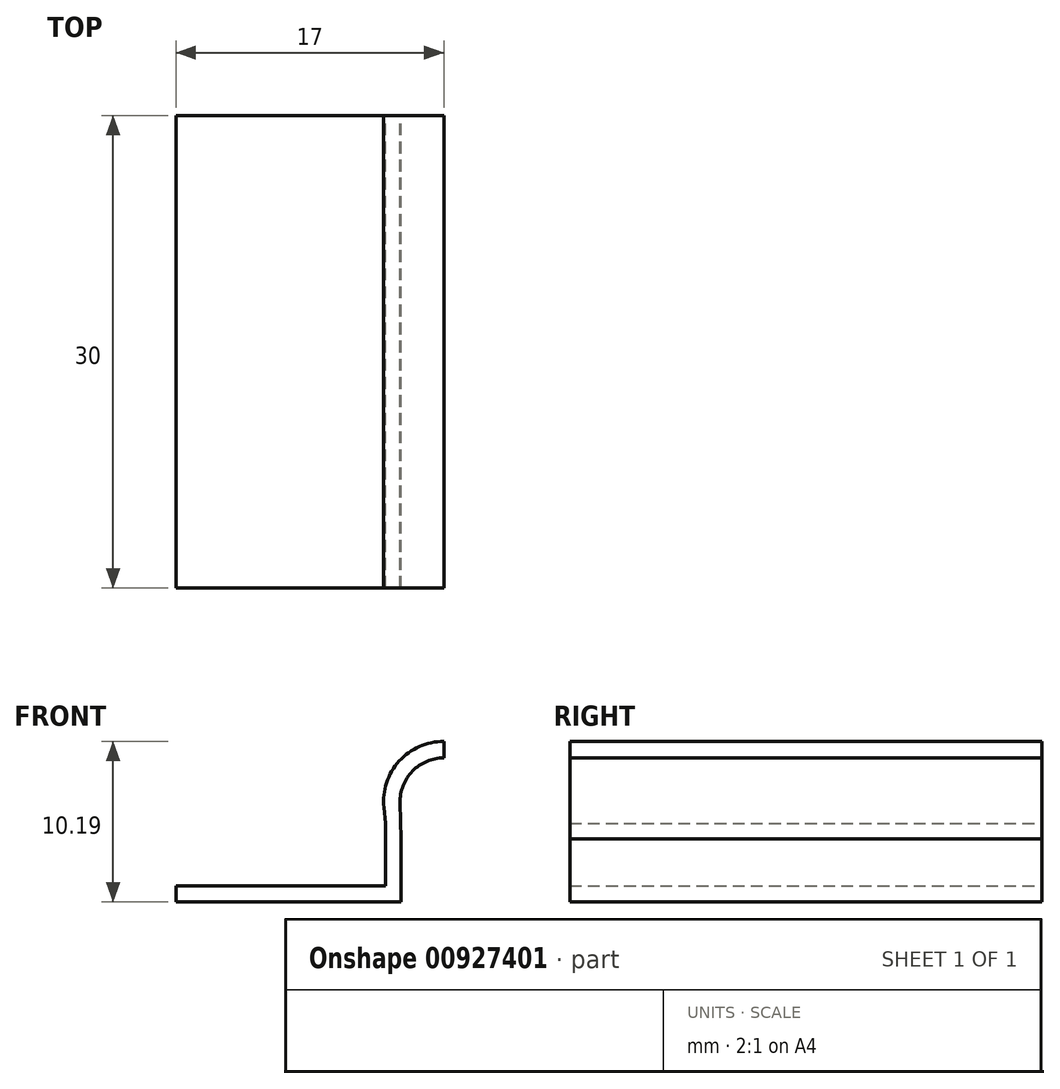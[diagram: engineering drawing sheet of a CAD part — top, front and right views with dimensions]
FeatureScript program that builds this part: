
annotation { "Feature Type Name" : "Feature", "Feature Type Description" : "" }
export const myFeature = defineFeature(function(context is Context, id is Id, definition is map)
    precondition{}
    {
        {
            var Q0;
            Q0=qCreatedBy(makeId("Front.planeOp"),FACE);
            var sketch = newSketch(context, id + "F0", { "sketchPlane" : qUnion([Q0])});
            skLineSegment(sketch, "E0.right", {"start": v(-17, -0.5) * mm, "end": v(-17, 0.5) * mm});
            skPoint(sketch, "E0.middle", {"position": v(0, 0) * mm});
            skLineSegment(sketch, "E1.right", {"start": v(-2.7, -0.5) * mm, "end": v(-2.7, 3.5) * mm});
            skLineSegment(sketch, "E2.top", {"start": v(-3.7, -0.5) * mm, "end": v(-2.7, -0.5) * mm});
            skLineSegment(sketch, "E2.left", {"start": v(-3.7, 4.5) * mm, "end": v(-3.7, 0.5) * mm});
            skLineSegment(sketch, "E3", {"start": v(3.57, 4.5) * mm, "end": v(3.57, 4.5) * mm});
            skLineSegment(sketch, "E4", {"start": v(-3.7, 4.5) * mm, "end": v(-3.8, 5.5) * mm});
            skArc(sketch, "E5", {"start": v(0, 8.64) * mm, "mid": v(-1.99, 7.8) * mm, "end": v(-2.77, 5.8) * mm});
            skLineSegment(sketch, "E6", {"start": v(-2.7, 3.5) * mm, "end": v(-2.77, 5.8) * mm});
            skLineSegment(sketch, "E7.trimOffspring", {"start": v(-3.7, 0.5) * mm, "end": v(-17, 0.5) * mm});
            skLineSegment(sketch, "E8.trimOffspring", {"start": v(-2.7, -0.5) * mm, "end": v(-17, -0.5) * mm});
            skArc(sketch, "E9.trimOffspring", {"start": v(0, 9.7) * mm, "mid": v(-2.83, 8.44) * mm, "end": v(-3.8, 5.5) * mm});
            skPoint(sketch, "E10", {"position": v(0, 9.7) * mm});
            skPoint(sketch, "E10.positionSnap0", {"position": v(0, 9.7) * mm});
            skPoint(sketch, "E11", {"position": v(0, 8.64) * mm});
            skLineSegment(sketch, "E12", {"start": v(0, 9.7) * mm, "end": v(0, 8.64) * mm});
            skSolve(sketch);
        }
        {
            var Q0;
            Q0 = qSketchRegion(id + "F0", true);
            extrude(context, id + "F1", {"entities" : qUnion([Q0]), "depth" : 30 * mm, "offsetDistance" : 25 * mm});
        }
    });
